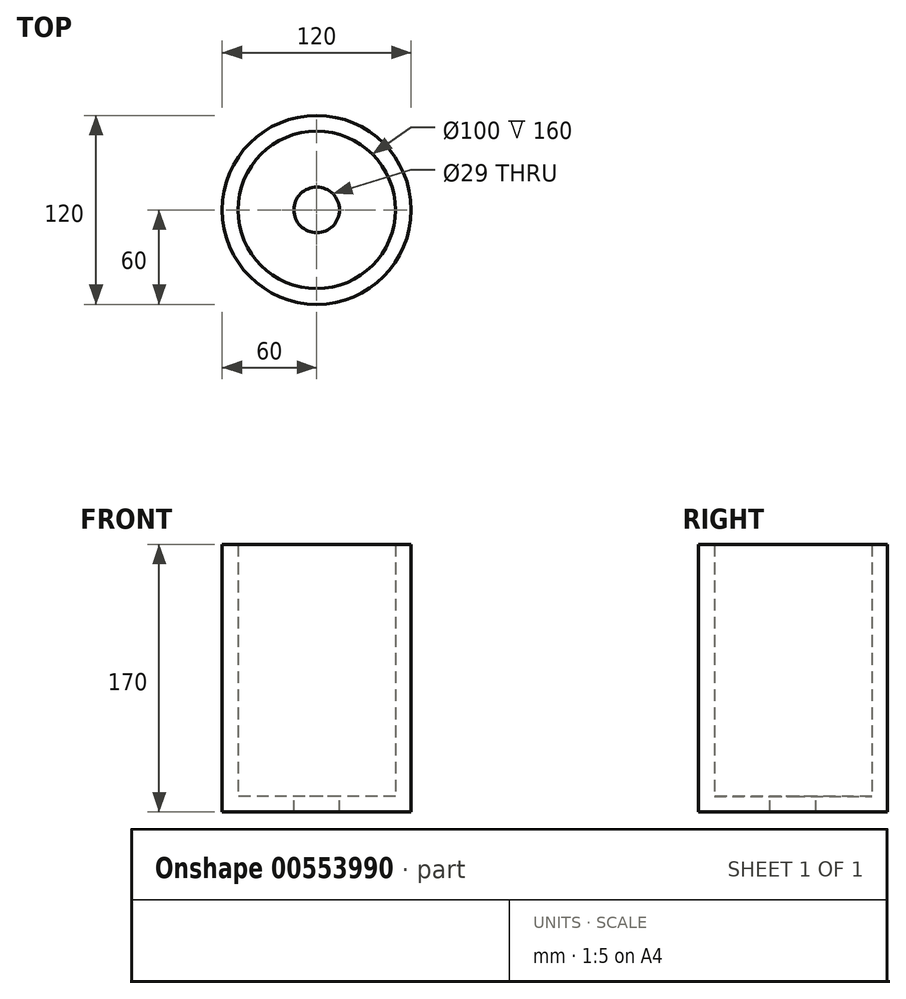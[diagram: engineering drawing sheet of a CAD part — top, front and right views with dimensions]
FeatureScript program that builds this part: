
annotation { "Feature Type Name" : "Feature", "Feature Type Description" : "" }
export const myFeature = defineFeature(function(context is Context, id is Id, definition is map)
    precondition{}
    {
        {
            var Q0;
            Q0=qCreatedBy(makeId("Top.planeOp"),FACE);
            var sketch = newSketch(context, id + "F0", { "sketchPlane" : qUnion([Q0])});
            skCircle(sketch, "E0", {"center": v(0, 0) * mm, "radius": 60 * mm});
            skSolve(sketch);
        }
        {
            var Q0;
            Q0 = qSketchRegion(id + "F0", true);
            extrude(context, id + "F1", {"entities" : qUnion([Q0]), "endBound" : BoundingType.SYMMETRIC, "depth" : 170 * mm, "offsetDistance" : 25 * mm});
        }
        {
            var Q0;
            Q0=makeQuery(id+"F1.opExtrude","CAP_FACE",FACE,{"disambiguationData":[OSD([sQuery(id+"F0.wireOp",EDGE,"E0")])],"isStart":false});
            shell(context, id + "F2", {"entities" : qUnion([Q0]), "thickness" : 10 * mm});
        }
        {
            var Q0;
            Q0=makeQuery(id+"F1.opExtrude","CAP_FACE",FACE,{"disambiguationData":[OSD([sQuery(id+"F0.wireOp",EDGE,"E0")])],"isStart":true});
            var sketch = newSketch(context, id + "F3", { "sketchPlane" : qUnion([Q0])});
            skCircle(sketch, "E1", {"center": v(0, 0) * mm, "radius": 14.5 * mm});
            skSolve(sketch);
        }
        {
            var Q0;
            Q0 = qSketchRegion(id + "F3", true);
            extrude(context, id + "F4", {"entities" : qUnion([Q0]), "operationType" : NewBodyOperationType.REMOVE, "endBound" : BoundingType.SYMMETRIC, "depth" : 50 * mm, "offsetDistance" : 25 * mm});
        }
    });
